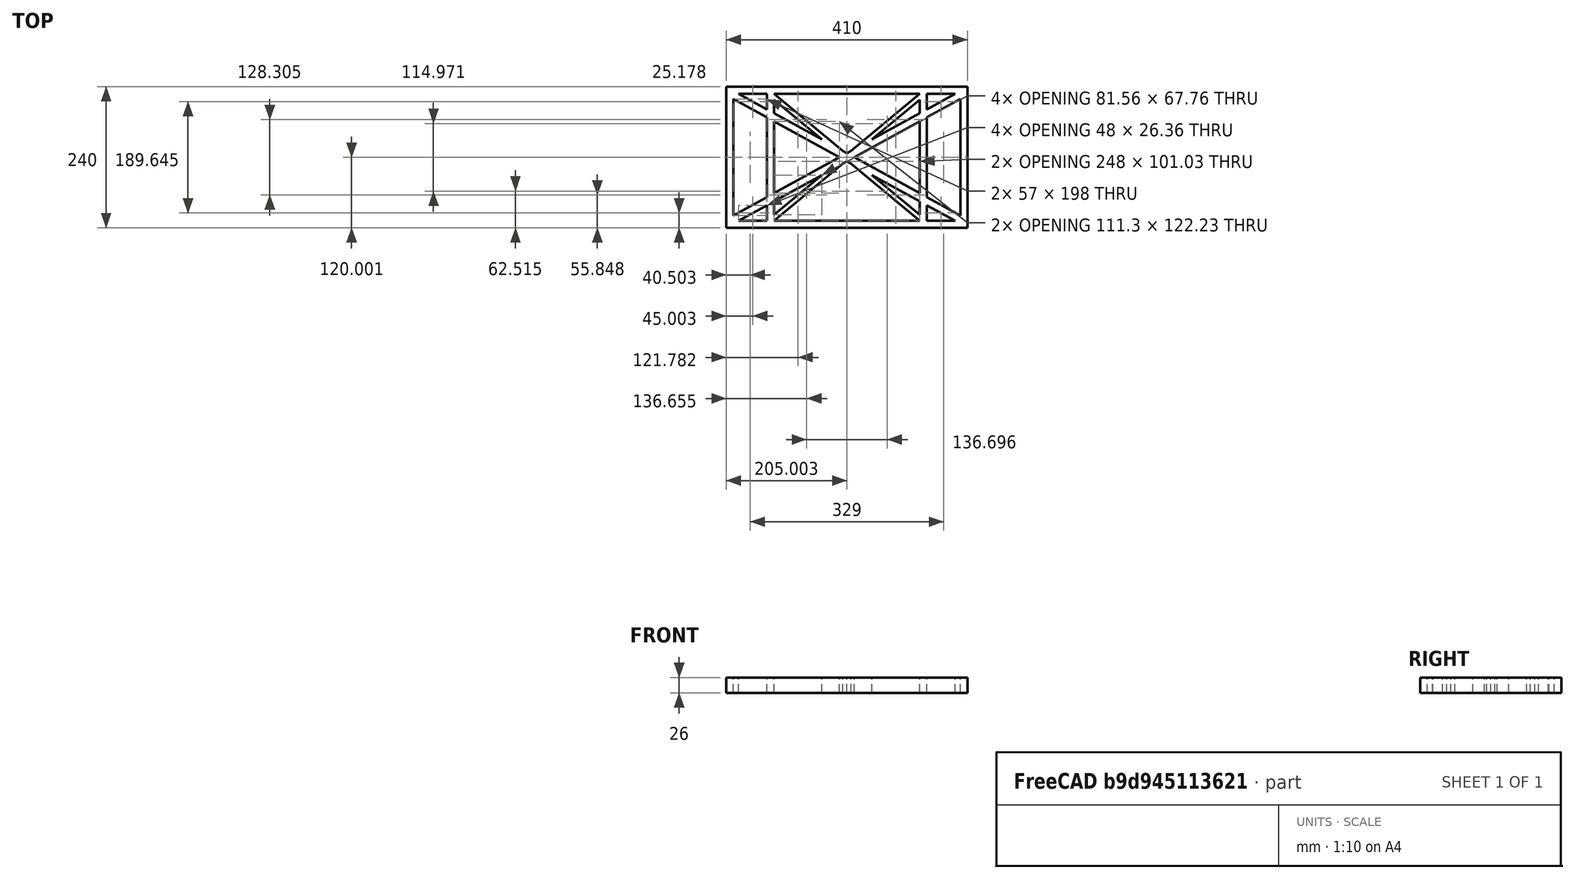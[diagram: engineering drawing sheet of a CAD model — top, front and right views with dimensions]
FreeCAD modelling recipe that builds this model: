
FCSTD DOCUMENT  (FreeCAD 0.19R0.19.2)
Label: laptopStand027
License: All rights reserved
LicenseURL: http://en.wikipedia.org/wiki/All_rights_reserved
objects: Sketcher::SketchObject×3, Part::Extrusion×1
note: 4 computed .brp shape members not serialized (recipe doc carries the construction recipe); baked Part::Feature solids carry a one-line shape summary decoded from their .brp

FEATURE [Sketcher::SketchObject] Sketch
  FullyConstrained = true
  sketch-geometry (52):
    g0: LineSegment StartX=-22.9272 StartY=136.221 StartZ=0 EndX=-22.9272 EndY=-103.779 EndZ=0
    g1: LineSegment StartX=-22.9272 StartY=136.221 StartZ=0 EndX=387.073 EndY=136.221 EndZ=0
    g2: LineSegment StartX=-22.9272 StartY=-103.779 StartZ=0 EndX=387.073 EndY=-103.779 EndZ=0
    g3: LineSegment StartX=387.073 StartY=136.221 StartZ=0 EndX=387.073 EndY=-103.779 EndZ=0
    g4: LineSegment StartX=375.073 StartY=115.221 StartZ=0 EndX=318.073 EndY=83.9235 EndZ=0
    g5: LineSegment StartX=-10.9272 StartY=-82.7794 StartZ=0 EndX=46.0728 EndY=-51.4823 EndZ=0
    g6: LineSegment StartX=-1.92719 StartY=124.221 StartZ=0 EndX=46.0728 EndY=97.8651 EndZ=0
    g7: LineSegment StartX=366.073 StartY=-91.7794 StartZ=0 EndX=318.073 EndY=-65.424 EndZ=0
    g8: LineSegment StartX=-10.9272 StartY=115.221 StartZ=0 EndX=-10.9272 EndY=-82.7794 EndZ=0
    g9: LineSegment StartX=375.073 StartY=-82.7794 StartZ=0 EndX=375.073 EndY=115.221 EndZ=0
    g10: LineSegment StartX=-1.92719 StartY=-91.7794 StartZ=0 EndX=46.0728 EndY=-91.7794 EndZ=0
    g11: LineSegment StartX=318.073 StartY=124.221 StartZ=0 EndX=366.073 EndY=124.221 EndZ=0
    g12: LineSegment StartX=306.073 StartY=-81.8102 StartZ=0 EndX=224.513 EndY=-14.0532 EndZ=0
    g13: LineSegment StartX=58.0728 StartY=114.251 StartZ=0 EndX=139.632 EndY=46.4944 EndZ=0
    g14: LineSegment StartX=306.073 StartY=124.221 StartZ=0 EndX=189.124 EndY=27.0628 EndZ=0
    g15: LineSegment StartX=58.0728 StartY=-91.7794 StartZ=0 EndX=175.022 EndY=5.37834 EndZ=0
    g16: LineSegment StartX=46.0728 StartY=124.221 StartZ=0 EndX=46.0728 EndY=97.8651 EndZ=0
    g17: LineSegment StartX=58.0728 StartY=-81.8102 StartZ=0 EndX=58.0728 EndY=-58.8351 EndZ=0
    g18: LineSegment StartX=318.073 StartY=124.221 StartZ=0 EndX=318.073 EndY=97.8651 EndZ=0
    g19: LineSegment StartX=306.073 StartY=114.251 StartZ=0 EndX=306.073 EndY=91.2763 EndZ=0
    g20: LineSegment StartX=182.073 StartY=23.1914 StartZ=0 EndX=189.124 EndY=27.0628 EndZ=0
    g21: LineSegment StartX=182.073 StartY=9.24976 StartZ=0 EndX=175.022 EndY=5.37834 EndZ=0
    g22: LineSegment StartX=224.513 StartY=46.4944 StartZ=0 EndX=306.073 EndY=114.251 EndZ=0
    g23: LineSegment StartX=175.022 StartY=27.0628 StartZ=0 EndX=58.0728 EndY=124.221 EndZ=0
    g24: LineSegment StartX=169.377 StartY=16.2206 StartZ=0 EndX=58.0728 EndY=77.3346 EndZ=0
    g25: LineSegment StartX=139.632 StartY=-14.0532 StartZ=0 EndX=58.0728 EndY=-81.8102 EndZ=0
    g26: LineSegment StartX=194.768 StartY=16.2206 StartZ=0 EndX=306.073 EndY=-44.8935 EndZ=0
    g27: LineSegment StartX=224.513 StartY=46.4944 StartZ=0 EndX=306.073 EndY=91.2763 EndZ=0
    g28: LineSegment StartX=175.022 StartY=27.0628 StartZ=0 EndX=182.073 EndY=23.1914 EndZ=0
    g29: LineSegment StartX=139.632 StartY=-14.0532 StartZ=0 EndX=58.0728 EndY=-58.8351 EndZ=0
    g30: LineSegment StartX=189.124 StartY=5.37834 StartZ=0 EndX=182.073 EndY=9.24976 EndZ=0
    g31: LineSegment StartX=189.124 StartY=5.37834 StartZ=0 EndX=306.073 EndY=-91.7794 EndZ=0
    g32: LineSegment StartX=306.073 StartY=77.3346 StartZ=0 EndX=306.073 EndY=-44.8935 EndZ=0
    g33: LineSegment StartX=318.073 StartY=83.9235 StartZ=0 EndX=318.073 EndY=-51.4823 EndZ=0
    g34: LineSegment StartX=318.073 StartY=97.8651 StartZ=0 EndX=366.073 EndY=124.221 EndZ=0
    g35: LineSegment StartX=306.073 StartY=77.3346 StartZ=0 EndX=194.768 EndY=16.2206 EndZ=0
    g36: LineSegment StartX=306.073 StartY=-58.8351 StartZ=0 EndX=224.513 EndY=-14.0532 EndZ=0
    g37: LineSegment StartX=306.073 StartY=-58.8351 StartZ=0 EndX=306.073 EndY=-81.8102 EndZ=0
    g38: LineSegment StartX=318.073 StartY=-51.4823 StartZ=0 EndX=375.073 EndY=-82.7794 EndZ=0
    g39: LineSegment StartX=318.073 StartY=-65.424 StartZ=0 EndX=318.073 EndY=-91.7794 EndZ=0
    g40: LineSegment StartX=306.073 StartY=124.221 StartZ=0 EndX=58.0728 EndY=124.221 EndZ=0
    g41: LineSegment StartX=318.073 StartY=-91.7794 StartZ=0 EndX=366.073 EndY=-91.7794 EndZ=0
    g42: LineSegment StartX=58.0728 StartY=-91.7794 StartZ=0 EndX=306.073 EndY=-91.7794 EndZ=0
    g43: LineSegment StartX=58.0728 StartY=-44.8935 StartZ=0 EndX=58.0728 EndY=77.3346 EndZ=0
    g44: LineSegment StartX=46.0728 StartY=-65.424 StartZ=0 EndX=-1.92719 EndY=-91.7794 EndZ=0
    g45: LineSegment StartX=46.0728 StartY=-65.424 StartZ=0 EndX=46.0728 EndY=-91.7794 EndZ=0
    g46: LineSegment StartX=58.0728 StartY=-44.8935 StartZ=0 EndX=169.377 EndY=16.2206 EndZ=0
    g47: LineSegment StartX=58.0728 StartY=91.2763 StartZ=0 EndX=58.0728 EndY=114.251 EndZ=0
    g48: LineSegment StartX=46.0728 StartY=83.9235 StartZ=0 EndX=46.0728 EndY=-51.4823 EndZ=0
    g49: LineSegment StartX=46.0728 StartY=124.221 StartZ=0 EndX=-1.92719 EndY=124.221 EndZ=0
    g50: LineSegment StartX=58.0728 StartY=91.2763 StartZ=0 EndX=139.632 EndY=46.4944 EndZ=0
    g51: LineSegment StartX=46.0728 StartY=83.9235 StartZ=0 EndX=-10.9272 EndY=115.221 EndZ=0
  constraints (102):
    c: Vertical(g0)
    c: Distance(g0) = 240
    c: Horizontal(g1)
    c: Distance(g1) = 410
    c: Coincident(g1,g0)
    c: Coincident(g2,g0)
    c: Horizontal(g2)
    c: Coincident(g3,g1)
    c: Vertical(g3)
    c: Coincident(g2,g3)
    c: Block(g1)
    c: Horizontal(g10)
    c: Horizontal(g11)
    c: PointOnObject(g35,g6)
    c: Coincident(g28,g20)
    c: Coincident(g30,g21)
    c: Tangent(g7,g24)
    c: PointOnObject(g24,g5)
    c: PointOnObject(g26,g4)
    c: Coincident(g20,g14)
    c: Tangent(g20,g27)
    c: Coincident(g50,g13)
    c: Coincident(g28,g23)
    c: Coincident(g22,g27)
    c: Coincident(g21,g15)
    c: Coincident(g29,g25)
    c: Tangent(g21,g29)
    c: Coincident(g36,g12)
    c: Coincident(g31,g30)
    c: Coincident(g22,g19)
    c: Tangent(g19,g32)
    c: Tangent(g18,g33)
    c: Coincident(g27,g19)
    c: Tangent(g27,g34)
    c: Coincident(g4,g33)
    c: Coincident(g35,g32)
    c: Tangent(g4,g35)
    c: Coincident(g37,g12)
    c: Tangent(g7,g36)
    c: Tangent(g32,g37)
    c: Coincident(g26,g32)
    c: Tangent(g26,g38)
    c: Coincident(g33,g38)
    c: Coincident(g39,g7)
    c: Tangent(g33,g39)
    c: Coincident(g25,g17)
    c: Tangent(g17,g43)
    c: Coincident(g29,g17)
    c: Tangent(g29,g44)
    c: Coincident(g45,g44)
    c: Tangent(g16,g45)
    c: Coincident(g5,g48)
    c: Coincident(g46,g43)
    c: Tangent(g5,g46)
    c: Tangent(g43,g47)
    c: Tangent(g16,g48)
    c: Coincident(g13,g47)
    c: PointOnObject(g40,g23)
    c: Tangent(g40,g49)
    c: Coincident(g6,g16)
    c: Coincident(g50,g47)
    c: Tangent(g6,g50)
    c: Coincident(g24,g43)
    c: Coincident(g51,g48)
    c: Tangent(g24,g51)
    c: Block(g23)
    c: Block(g14)
    c: Block(g20)
    c: Block(g40)
    c: Block(g18)
    c: Block(g34)
    c: Block(g4)
    c: Block(g38)
    c: Block(g9)
    c: Block(g36)
    c: Block(g37)
    c: Block(g7)
    c: Block(g39)
    c: Block(g22)
    c: Block(g31)
    c: Block(g42)
    c: Block(g21)
    c: Block(g15)
    c: Block(g29)
    c: Block(g25)
    c: Block(g45)
    c: Block(g44)
    c: Block(g5)
    c: Block(g8)
    c: Block(g51)
    c: Block(g6)
    c: Block(g16)
    c: Block(g13)
    c: Block(g47)
    c: Block(g35)
    c: Block(g32)
    c: Block(g24)
    c: Block(g46)
    c: Block(g49)
    c: Block(g11)
    c: Block(g41)
    c: Block(g10)
FEATURE [Part::Extrusion] Extrude
  Base = -> Sketch
  Dir = (0,0,1)
  DirMode = 2
  FaceMakerClass = Part::FaceMakerBullseye
  LengthFwd = 26
  LengthRev = 0
  Solid = true
  Symmetric = false
FEATURE [Sketcher::SketchObject] Sketch001
  FullyConstrained = true
  MapMode = 4
  Placement = pos=(0,0,0) rot=(0.57735,0.57735,0.57735;2.0944rad)
  Support = -> [Sketch]
  sketch-geometry (25):
    g0: LineSegment StartX=17.2228 StartY=-16.0875 StartZ=0 EndX=117.223 EndY=-16.0875 EndZ=0
    g1: LineSegment StartX=17.2228 StartY=-16.0875 StartZ=0 EndX=17.2228 EndY=-19.0875 EndZ=0
    g2: LineSegment StartX=117.223 StartY=-16.0875 StartZ=0 EndX=117.223 EndY=-19.0875 EndZ=0
    g3: BSplineCurve PolesCount=3 KnotsCount=2 Degree=2 IsPeriodic=0
    g4: LineSegment StartX=94.6577 StartY=-26.1351 StartZ=0 EndX=24.2583 EndY=-213.335 EndZ=0
    g5: LineSegment StartX=-9.4377 StartY=-200.664 StartZ=0 EndX=24.2583 EndY=-213.335 EndZ=0
    g6: LineSegment StartX=-9.4377 StartY=-200.664 StartZ=0 EndX=56.1962 EndY=-26.1351 EndZ=0
    g7: LineSegment StartX=17.2228 StartY=-19.0875 StartZ=0 EndX=38.8094 EndY=-19.0875 EndZ=0
    g8: BSplineCurve PolesCount=4 KnotsCount=2 Degree=3 IsPeriodic=0
    g9: ArcOfCircle CenterX=73.122 CenterY=-32.2909 CenterZ=0 NormalX=0 NormalY=0 NormalZ=1 AngleXU=0 Radius=13 StartAngle=5.92268 EndAngle=9.06428
    g10: LineSegment StartX=85.2864 StartY=-36.8765 StartZ=0 EndX=78.9505 EndY=-53.7246 EndZ=0
    g11: LineSegment StartX=60.9577 StartY=-27.7052 StartZ=0 EndX=54.6191 EndY=-44.5532 EndZ=0
    g12: ArcOfCircle CenterX=66.7816 CenterY=-49.1439 CenterZ=0 NormalX=0 NormalY=0 NormalZ=1 AngleXU=0 Radius=13 StartAngle=2.78068 EndAngle=5.92131
    g13: ArcOfCircle CenterX=55.9263 CenterY=-78.1807 CenterZ=0 NormalX=0 NormalY=0 NormalZ=1 AngleXU=0 Radius=13 StartAngle=5.92268 EndAngle=9.06428
    g14: LineSegment StartX=68.0907 StartY=-82.7664 StartZ=0 EndX=61.7547 EndY=-99.6148 EndZ=0
    g15: ArcOfCircle CenterX=49.5884 CenterY=-95.0342 CenterZ=0 NormalX=0 NormalY=0 NormalZ=1 AngleXU=0 Radius=13 StartAngle=2.78068 EndAngle=5.92131
    g16: LineSegment StartX=43.7619 StartY=-73.595 StartZ=0 EndX=37.426 EndY=-90.4435 EndZ=0
    g17: ArcOfCircle CenterX=38.7206 CenterY=-124.067 CenterZ=0 NormalX=0 NormalY=0 NormalZ=1 AngleXU=0 Radius=13 StartAngle=5.92268 EndAngle=9.06428
    g18: LineSegment StartX=26.5562 StartY=-119.481 StartZ=0 EndX=20.2251 EndY=-136.329 EndZ=0
    g19: ArcOfCircle CenterX=32.3875 CenterY=-140.92 CenterZ=0 NormalX=0 NormalY=0 NormalZ=1 AngleXU=0 Radius=13 StartAngle=2.78068 EndAngle=5.92131
    g20: LineSegment StartX=50.885 StartY=-128.652 StartZ=0 EndX=44.549 EndY=-145.5 EndZ=0
    g21: ArcOfCircle CenterX=21.4715 CenterY=-169.934 CenterZ=0 NormalX=0 NormalY=0 NormalZ=1 AngleXU=0 Radius=13 StartAngle=5.92268 EndAngle=9.06428
    g22: LineSegment StartX=9.3071 StartY=-165.349 StartZ=0 EndX=2.97115 EndY=-182.197 EndZ=0
    g23: ArcOfCircle CenterX=15.1336 CenterY=-186.787 CenterZ=0 NormalX=0 NormalY=0 NormalZ=1 AngleXU=0 Radius=13 StartAngle=2.78068 EndAngle=5.92131
    g24: LineSegment StartX=33.6358 StartY=-174.52 StartZ=0 EndX=27.2999 EndY=-191.368 EndZ=0
  constraints (51):
    c: Horizontal(g0)
    c: Distance(g0) = 100
    c: Block(g0)
    c: Coincident(g1,g0)
    c: Vertical(g1)
    c: Distance(g1) = 3
    c: Coincident(g2,g0)
    c: Vertical(g2)
    c: Distance(g2) = 3
    c: Block(g3)
    c: Coincident(g3,g2)
    c: Coincident(g4,g3)
    c: Block(g4)
    c: Coincident(g5,g4)
    c: Coincident(g6,g5)
    c: Coincident(g7,g1)
    c: Horizontal(g7)
    c: Block(g8)
    c: Coincident(g8,g7)
    c: Coincident(g8,g6)
    c: Block(g6)
    c: Block(g9)
    c: Distance(g10) = 18
    c: Coincident(g10,g9)
    c: Parallel(g4,g10)
    c: Coincident(g11,g9)
    c: Block(g12)
    c: Coincident(g12,g11)
    c: Block(g11)
    c: Coincident(g14,g13)
    c: Coincident(g16,g13)
    c: Block(g15)
    c: Coincident(g15,g16)
    c: Block(g16)
    c: Block(g13)
    c: Block(g14)
    c: Coincident(g20,g17)
    c: Coincident(g18,g17)
    c: Block(g19)
    c: Coincident(g19,g18)
    c: Block(g18)
    c: Block(g17)
    c: Coincident(g24,g21)
    c: Coincident(g22,g21)
    c: Block(g23)
    c: Coincident(g23,g22)
    c: Block(g22)
    c: Block(g21)
    c: Distance(g24) = 18
    c: Block(g24)
    c: Block(g20)
FEATURE [Sketcher::SketchObject] Sketch002
  FullyConstrained = true
  Placement = pos=(0,0,0) rot=(-1,0,0;4.71239rad)
